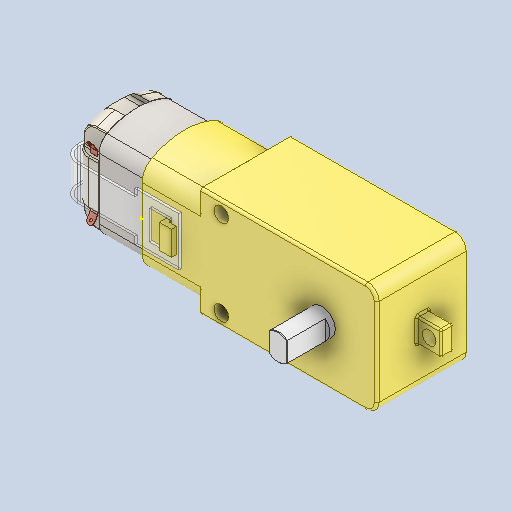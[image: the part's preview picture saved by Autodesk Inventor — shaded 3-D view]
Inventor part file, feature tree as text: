
AUTODESK INVENTOR PART (.ipt)
format: ipt  version: 2023 (Build 270158000, 158)  size: 560,128 bytes
history: mixed  units: mm
features: other x3, fillet x2, sketch x1, chamfer x1, mirror x1, imported_body x1
ambient origin geometry x8: Origin, YZ Plane, XZ Plane, XY Plane, X Axis, Y Axis, Z Axis, Center Point
bodies: Solid1 (imported_parasolid), Solid3 (imported_parasolid), Solid5 (imported_parasolid), Solid6 (imported_parasolid), Solid7 (imported_parasolid), Solid8 (imported_parasolid), Solid9 (imported_parasolid)
feature tree (9):
  sketch  "Sketch1"
  other  "Cortar-Extruir7"
  fillet  "Redondeo2"  [1 undecoded]
  fillet  "Redondeo14"  [1 undecoded]
  chamfer  "Chaflán1"  [1 undecoded]
  other  "Cortar-Extruir9[1]"
  other  "Cortar-Extruir9[2]"
  mirror  "Simetría2"
  imported_body  NMx_Import_Brep_tag  [imported B-rep: ~66 faces, bbox_mm=[64.2, 18.598921, 27.3]]
note: 3 required parameter values undecoded (feature->parameter linkage not recoverable at this tier; creation-order binding heuristic only, values carry confidence <= 0.55)
